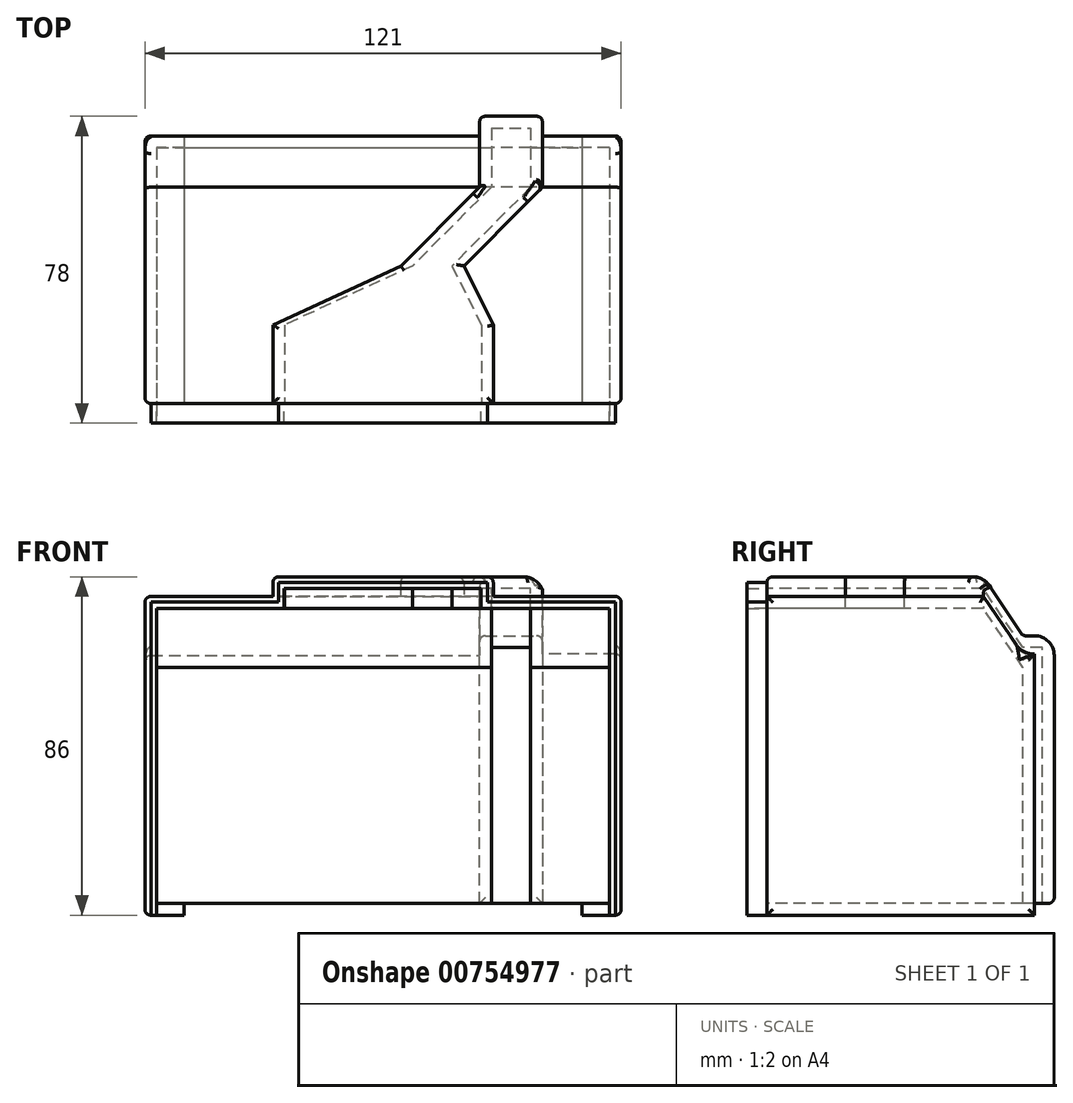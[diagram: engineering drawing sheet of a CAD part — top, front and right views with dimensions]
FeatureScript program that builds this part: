
annotation { "Feature Type Name" : "Feature", "Feature Type Description" : "" }
export const myFeature = defineFeature(function(context is Context, id is Id, definition is map)
    precondition{}
    {
        {
            var Q0;
            Q0=qCreatedBy(makeId("Front.planeOp"),FACE);
            var sketch = newSketch(context, id + "F0", { "sketchPlane" : qUnion([Q0])});
            skLineSegment(sketch, "E0", {"start": v(88, 68) * mm, "end": v(78, 68) * mm});
            skLineSegment(sketch, "E1", {"start": v(75, 71) * mm, "end": v(91, 71) * mm});
            skLineSegment(sketch, "E2", {"start": v(75, 3) * mm, "end": v(78, 3) * mm});
            skLineSegment(sketch, "E3", {"start": v(88, 3) * mm, "end": v(91, 3) * mm});
            skLineSegment(sketch, "E4", {"start": v(75, 3) * mm, "end": v(75, 71) * mm});
            skLineSegment(sketch, "E5", {"start": v(78, 3) * mm, "end": v(78, 68) * mm});
            skLineSegment(sketch, "E6", {"start": v(88, 3) * mm, "end": v(88, 68) * mm});
            skLineSegment(sketch, "E7", {"start": v(91, 71) * mm, "end": v(91, 3) * mm});
            skLineSegment(sketch, "E8", {"start": v(0, 0) * mm, "end": v(75, 0) * mm, "construction": true});
            skLineSegment(sketch, "E9", {"start": v(75, 0) * mm, "end": v(75, 3) * mm, "construction": true});
            skSolve(sketch);
        }
        {
            var Q0;
            Q0=makeQuery(id+"F0.imprint","IMPRINT",FACE,{"disambiguationData":[TD([[makeQuery(id+"F0.imprint","IMPRINT",EDGE,{"derivedFrom":sQuery(id+"F0.wireOp",EDGE,"E0")}),-1.0]])]});
            var sketch = newSketch(context, id + "F1", { "sketchPlane" : qUnion([Q0])});
            skLineSegment(sketch, "E10.0.0", {"start": v(91, 71) * mm, "end": v(75, 71) * mm});
            skLineSegment(sketch, "E10.0.1", {"start": v(75, 71) * mm, "end": v(75, 3) * mm});
            skLineSegment(sketch, "E10.0.7", {"start": v(91, 3) * mm, "end": v(91, 71) * mm});
            skLineSegment(sketch, "E11", {"start": v(91, 3) * mm, "end": v(75, 3) * mm});
            skSolve(sketch);
        }
        {
            var Q0;
            Q0 = qSketchRegion(id + "F1", true);
            extrude(context, id + "F2", {"entities" : qUnion([Q0]), "oppositeDirection" : true, "depth" : 3 * mm, "offsetDistance" : 25 * mm});
        }
        {
            var Q0;
            Q0=makeQuery(id+"F0.imprint","IMPRINT",FACE,{"disambiguationData":[TD([[makeQuery(id+"F0.imprint","IMPRINT",EDGE,{"derivedFrom":sQuery(id+"F0.wireOp",EDGE,"E0")}),-1.0]])]});
            cPlane(context, id + "F3", {"entities" : qUnion([Q0]), "cplaneType" : CPlaneType.OFFSET, "offset" : 5 * mm, "width" : 150 * mm, "height" : 150 * mm});
        }
        {
            var Q0;
            Q0=qCreatedBy(id+"F3.planeOp",FACE);
            var sketch = newSketch(context, id + "F4", { "sketchPlane" : qUnion([Q0])});
            skLineSegment(sketch, "E12", {"start": v(88, 68) * mm, "end": v(78, 68) * mm});
            skLineSegment(sketch, "E13", {"start": v(75, 71) * mm, "end": v(91, 71) * mm});
            skLineSegment(sketch, "E14", {"start": v(75, 3) * mm, "end": v(78, 3) * mm});
            skLineSegment(sketch, "E15", {"start": v(88, 3) * mm, "end": v(91, 3) * mm});
            skLineSegment(sketch, "E16", {"start": v(75, 3) * mm, "end": v(75, 71) * mm});
            skLineSegment(sketch, "E17", {"start": v(78, 3) * mm, "end": v(78, 68) * mm});
            skLineSegment(sketch, "E18", {"start": v(88, 3) * mm, "end": v(88, 68) * mm});
            skLineSegment(sketch, "E19", {"start": v(91, 71) * mm, "end": v(91, 3) * mm});
            skLineSegment(sketch, "E20", {"start": v(0, 0) * mm, "end": v(75, 0) * mm, "construction": true});
            skLineSegment(sketch, "E21", {"start": v(75, 0) * mm, "end": v(75, 3) * mm, "construction": true});
            skSolve(sketch);
        }
        {
            var Q1;
            Q1=makeQuery(id+"F1.imprint","IMPRINT",FACE,{"disambiguationData":[TD([[makeQuery(id+"F1.imprint","IMPRINT",EDGE,{"derivedFrom":sQuery(id+"F1.wireOp",EDGE,"E10.0.0")}),-1.0]])]});
            var Q2;
            Q2=makeQuery(id+"F4.imprint","IMPRINT",FACE,{"disambiguationData":[TD([[makeQuery(id+"F4.imprint","IMPRINT",EDGE,{"derivedFrom":sQuery(id+"F4.wireOp",EDGE,"E12")}),-1.0]])]});
            loft(context, id + "F5", {"operationType" : NewBodyOperationType.ADD, "sheetProfilesArray" : [{ "sheetProfileEntities" : qUnion([Q1]) }, { "sheetProfileEntities" : qUnion([Q2]) }]});
        }
        {
            var Q0;
            Q0=qCreatedBy(id+"F3.planeOp",FACE);
            var sketch = newSketch(context, id + "F6", { "sketchPlane" : qUnion([Q0])});
            skLineSegment(sketch, "E22", {"start": v(0, 3) * mm, "end": v(-7, 3) * mm});
            skLineSegment(sketch, "E23", {"start": v(-7, 3) * mm, "end": v(-7, 63) * mm});
            skLineSegment(sketch, "E24", {"start": v(108, 63) * mm, "end": v(108, 3) * mm});
            skLineSegment(sketch, "E25", {"start": v(108, 3) * mm, "end": v(101, 3) * mm});
            skLineSegment(sketch, "E26", {"start": v(101, 3) * mm, "end": v(101, 0) * mm});
            skLineSegment(sketch, "E27", {"start": v(101, 0) * mm, "end": v(111, 0) * mm});
            skLineSegment(sketch, "E28", {"start": v(111, 0) * mm, "end": v(111, 66.4) * mm});
            skLineSegment(sketch, "E29", {"start": v(-10, 66) * mm, "end": v(-10, 0) * mm});
            skLineSegment(sketch, "E30", {"start": v(-10, 0) * mm, "end": v(0, 0) * mm});
            skLineSegment(sketch, "E31", {"start": v(0, 0) * mm, "end": v(0, 3) * mm});
            skLineSegment(sketch, "E32", {"start": v(88, 68) * mm, "end": v(78, 68) * mm});
            skLineSegment(sketch, "E33", {"start": v(75, 71) * mm, "end": v(91, 71) * mm});
            skLineSegment(sketch, "E34", {"start": v(111, 66.4) * mm, "end": v(91, 66.4) * mm});
            skLineSegment(sketch, "E35", {"start": v(-10, 66) * mm, "end": v(75, 66) * mm});
            skLineSegment(sketch, "E36", {"start": v(75, 66) * mm, "end": v(75, 71) * mm});
            skLineSegment(sketch, "E37", {"start": v(91, 66.4) * mm, "end": v(91, 71) * mm});
            skLineSegment(sketch, "E38", {"start": v(108, 63) * mm, "end": v(88, 63) * mm});
            skLineSegment(sketch, "E39", {"start": v(88, 63) * mm, "end": v(88, 68) * mm});
            skLineSegment(sketch, "E40", {"start": v(-7, 63) * mm, "end": v(78, 63) * mm});
            skLineSegment(sketch, "E41", {"start": v(78, 63) * mm, "end": v(78, 68) * mm});
            skSolve(sketch);
        }
        {
            var Q0;
            Q0=makeQuery(id+"F6.imprint","IMPRINT",FACE,{"disambiguationData":[TD([[makeQuery(id+"F6.imprint","IMPRINT",EDGE,{"derivedFrom":sQuery(id+"F6.wireOp",EDGE,"E22")}),1.0]])]});
            var sketch = newSketch(context, id + "F7", { "sketchPlane" : qUnion([Q0])});
            skPoint(sketch, "E42.0", {"position": v(-10, 66) * mm});
            skPoint(sketch, "E43.0", {"position": v(75, 66) * mm});
            skPoint(sketch, "E44.0", {"position": v(91, 66.4) * mm});
            skPoint(sketch, "E45.0", {"position": v(101, 3) * mm});
            skPoint(sketch, "E46.0", {"position": v(111, 66.4) * mm});
            skLineSegment(sketch, "E47", {"start": v(-10, 66) * mm, "end": v(-10, 3) * mm});
            skLineSegment(sketch, "E48", {"start": v(75, 3) * mm, "end": v(75, 66) * mm});
            skLineSegment(sketch, "E49", {"start": v(75, 66) * mm, "end": v(-10, 66) * mm});
            skLineSegment(sketch, "E50", {"start": v(91, 66.4) * mm, "end": v(91, 3) * mm});
            skLineSegment(sketch, "E51", {"start": v(111, 3) * mm, "end": v(111, 66.4) * mm});
            skLineSegment(sketch, "E52", {"start": v(91, 66.4) * mm, "end": v(111, 66.4) * mm});
            skLineSegment(sketch, "E53", {"start": v(111, 3) * mm, "end": v(111, 0) * mm});
            skLineSegment(sketch, "E54", {"start": v(111, 0) * mm, "end": v(101, 0) * mm});
            skLineSegment(sketch, "E55", {"start": v(101, 0) * mm, "end": v(101, 3) * mm});
            skLineSegment(sketch, "E56", {"start": v(-10, 3) * mm, "end": v(-10, 0) * mm});
            skLineSegment(sketch, "E57", {"start": v(-10, 0) * mm, "end": v(0, 0) * mm});
            skLineSegment(sketch, "E58", {"start": v(0, 0) * mm, "end": v(0, 3) * mm});
            skLineSegment(sketch, "E59", {"start": v(101, 3) * mm, "end": v(91, 3) * mm});
            skLineSegment(sketch, "E60", {"start": v(75, 3) * mm, "end": v(0, 3) * mm});
            skSolve(sketch);
        }
        {
            var Q0;
            Q0=makeQuery(id+"F6.imprint","IMPRINT",FACE,{"disambiguationData":[TD([[makeQuery(id+"F6.imprint","IMPRINT",EDGE,{"derivedFrom":sQuery(id+"F6.wireOp",EDGE,"E22")}),1.0]])]});
            cPlane(context, id + "F8", {"entities" : qUnion([Q0]), "cplaneType" : CPlaneType.OFFSET, "offset" : 10 * mm, "width" : 150 * mm, "height" : 150 * mm});
        }
        {
            var Q0;
            Q0=qCreatedBy(id+"F8.planeOp",FACE);
            var sketch = newSketch(context, id + "F9", { "sketchPlane" : qUnion([Q0])});
            skLineSegment(sketch, "E61", {"start": v(0, 3) * mm, "end": v(-7, 3) * mm});
            skLineSegment(sketch, "E62", {"start": v(-7, 3) * mm, "end": v(-7, 78) * mm});
            skLineSegment(sketch, "E63", {"start": v(108, 78) * mm, "end": v(108, 3) * mm});
            skLineSegment(sketch, "E64", {"start": v(108, 3) * mm, "end": v(101, 3) * mm});
            skLineSegment(sketch, "E65", {"start": v(101, 3) * mm, "end": v(101, 0) * mm});
            skLineSegment(sketch, "E66", {"start": v(101, 0) * mm, "end": v(111, 0) * mm});
            skLineSegment(sketch, "E67", {"start": v(111, 0) * mm, "end": v(111, 81) * mm});
            skLineSegment(sketch, "E68", {"start": v(-10, 81) * mm, "end": v(-10, 0) * mm});
            skLineSegment(sketch, "E69", {"start": v(-10, 0) * mm, "end": v(0, 0) * mm});
            skLineSegment(sketch, "E70", {"start": v(0, 0) * mm, "end": v(0, 3) * mm});
            skLineSegment(sketch, "E71", {"start": v(-10, 81) * mm, "end": v(75, 81) * mm});
            skLineSegment(sketch, "E72", {"start": v(75, 81) * mm, "end": v(75, 86) * mm});
            skLineSegment(sketch, "E73", {"start": v(75, 86) * mm, "end": v(91, 86) * mm});
            skLineSegment(sketch, "E74", {"start": v(91, 86) * mm, "end": v(91, 81) * mm});
            skLineSegment(sketch, "E75", {"start": v(91, 81) * mm, "end": v(111, 81) * mm});
            skLineSegment(sketch, "E76", {"start": v(108, 78) * mm, "end": v(88, 78) * mm});
            skLineSegment(sketch, "E77", {"start": v(88, 78) * mm, "end": v(88, 83) * mm});
            skLineSegment(sketch, "E78", {"start": v(88, 83) * mm, "end": v(78, 83) * mm});
            skLineSegment(sketch, "E79", {"start": v(78, 83) * mm, "end": v(78, 78) * mm});
            skLineSegment(sketch, "E80", {"start": v(78, 78) * mm, "end": v(-7, 78) * mm});
            skSolve(sketch);
        }
        {
            var Q1;
            Q1=makeQuery(id+"F6.imprint","IMPRINT",FACE,{"disambiguationData":[TD([[makeQuery(id+"F6.imprint","IMPRINT",EDGE,{"derivedFrom":sQuery(id+"F6.wireOp",EDGE,"E22")}),1.0]])]});
            var Q2;
            Q2=makeQuery(id+"F9.imprint","IMPRINT",FACE,{"disambiguationData":[TD([[makeQuery(id+"F9.imprint","IMPRINT",EDGE,{"derivedFrom":sQuery(id+"F9.wireOp",EDGE,"E61")}),1.0]])]});
            loft(context, id + "F10", {"operationType" : NewBodyOperationType.ADD, "sheetProfilesArray" : [{ "sheetProfileEntities" : qUnion([Q1]) }, { "sheetProfileEntities" : qUnion([Q2]) }]});
        }
        {
            var Q0;
            Q0 = qSketchRegion(id + "F7", true);
            extrude(context, id + "F11", {"entities" : qUnion([Q0]), "operationType" : NewBodyOperationType.ADD, "oppositeDirection" : true, "depth" : 3 * mm, "offsetDistance" : 25 * mm});
        }
        {
            var Q0;
            Q0=makeQuery(id+"F9.imprint","IMPRINT",FACE,{"disambiguationData":[TD([[makeQuery(id+"F9.imprint","IMPRINT",EDGE,{"derivedFrom":sQuery(id+"F9.wireOp",EDGE,"E61")}),1.0]])]});
            cPlane(context, id + "F12", {"entities" : qUnion([Q0]), "cplaneType" : CPlaneType.OFFSET, "offset" : 20 * mm, "width" : 150 * mm, "height" : 150 * mm});
        }
        {
            var Q0;
            Q0=qCreatedBy(id+"F12.planeOp",FACE);
            var sketch = newSketch(context, id + "F13", { "sketchPlane" : qUnion([Q0])});
            skLineSegment(sketch, "E81", {"start": v(0, 3) * mm, "end": v(-7, 3) * mm});
            skLineSegment(sketch, "E82", {"start": v(-7, 3) * mm, "end": v(-7, 78) * mm});
            skLineSegment(sketch, "E83", {"start": v(108, 78) * mm, "end": v(108, 3) * mm});
            skLineSegment(sketch, "E84", {"start": v(108, 3) * mm, "end": v(101, 3) * mm});
            skLineSegment(sketch, "E85", {"start": v(101, 3) * mm, "end": v(101, 0) * mm});
            skLineSegment(sketch, "E86", {"start": v(101, 0) * mm, "end": v(111, 0) * mm});
            skLineSegment(sketch, "E87", {"start": v(111, 0) * mm, "end": v(111, 81) * mm});
            skLineSegment(sketch, "E88", {"start": v(-10, 81) * mm, "end": v(-10, 0) * mm});
            skLineSegment(sketch, "E89", {"start": v(-10, 0) * mm, "end": v(0, 0) * mm});
            skLineSegment(sketch, "E90", {"start": v(0, 0) * mm, "end": v(0, 3) * mm});
            skLineSegment(sketch, "E91", {"start": v(-10, 81) * mm, "end": v(55, 81) * mm});
            skLineSegment(sketch, "E92", {"start": v(55, 81) * mm, "end": v(55, 86) * mm});
            skLineSegment(sketch, "E93", {"start": v(55, 86) * mm, "end": v(71, 86) * mm});
            skLineSegment(sketch, "E94", {"start": v(71, 86) * mm, "end": v(71, 81) * mm});
            skLineSegment(sketch, "E95", {"start": v(71, 81) * mm, "end": v(111, 81) * mm});
            skLineSegment(sketch, "E96", {"start": v(108, 78) * mm, "end": v(68, 78) * mm});
            skLineSegment(sketch, "E97", {"start": v(68, 78) * mm, "end": v(68, 83) * mm});
            skLineSegment(sketch, "E98", {"start": v(68, 83) * mm, "end": v(58, 83) * mm});
            skLineSegment(sketch, "E99", {"start": v(58, 83) * mm, "end": v(58, 78) * mm});
            skLineSegment(sketch, "E100", {"start": v(58, 78) * mm, "end": v(-7, 78) * mm});
            skSolve(sketch);
        }
        {
            var Q1;
            Q1=makeQuery(id+"F9.imprint","IMPRINT",FACE,{"disambiguationData":[TD([[makeQuery(id+"F9.imprint","IMPRINT",EDGE,{"derivedFrom":sQuery(id+"F9.wireOp",EDGE,"E61")}),1.0]])]});
            var Q2;
            Q2=makeQuery(id+"F13.imprint","IMPRINT",FACE,{"disambiguationData":[TD([[makeQuery(id+"F13.imprint","IMPRINT",EDGE,{"derivedFrom":sQuery(id+"F13.wireOp",EDGE,"E81")}),1.0]])]});
            loft(context, id + "F14", {"operationType" : NewBodyOperationType.ADD, "sheetProfilesArray" : [{ "sheetProfileEntities" : qUnion([Q1]) }, { "sheetProfileEntities" : qUnion([Q2]) }]});
        }
        {
            var Q0;
            Q0=makeQuery(id+"F14.opLoft","CAP_FACE",FACE,{"disambiguationData":[OSD([makeQuery(id+"F13.imprint","IMPRINT",FACE,{"disambiguationData":[TD([[makeQuery(id+"F13.imprint","IMPRINT",EDGE,{"derivedFrom":sQuery(id+"F13.wireOp",EDGE,"E81")}),1.0]])]})])],"isStart":true});
            cPlane(context, id + "F15", {"entities" : qUnion([Q0]), "cplaneType" : CPlaneType.OFFSET, "offset" : 15 * mm, "width" : 150 * mm, "height" : 150 * mm});
        }
        {
            var Q0;
            Q0=qCreatedBy(id+"F15.planeOp",FACE);
            var sketch = newSketch(context, id + "F16", { "sketchPlane" : qUnion([Q0])});
            skLineSegment(sketch, "E101", {"start": v(0, 3) * mm, "end": v(-7, 3) * mm});
            skLineSegment(sketch, "E102", {"start": v(-7, 3) * mm, "end": v(-7, 78) * mm});
            skLineSegment(sketch, "E103", {"start": v(108, 78) * mm, "end": v(108, 3) * mm});
            skLineSegment(sketch, "E104", {"start": v(108, 3) * mm, "end": v(101, 3) * mm});
            skLineSegment(sketch, "E105", {"start": v(101, 3) * mm, "end": v(101, 0) * mm});
            skLineSegment(sketch, "E106", {"start": v(101, 0) * mm, "end": v(111, 0) * mm});
            skLineSegment(sketch, "E107", {"start": v(111, 0) * mm, "end": v(111, 81) * mm});
            skLineSegment(sketch, "E108", {"start": v(-10, 81) * mm, "end": v(-10, 0) * mm});
            skLineSegment(sketch, "E109", {"start": v(-10, 0) * mm, "end": v(0, 0) * mm});
            skLineSegment(sketch, "E110", {"start": v(0, 0) * mm, "end": v(0, 3) * mm});
            skLineSegment(sketch, "E111", {"start": v(-10, 81) * mm, "end": v(22.5, 81) * mm});
            skLineSegment(sketch, "E112", {"start": v(22.5, 81) * mm, "end": v(22.5, 86) * mm});
            skLineSegment(sketch, "E113", {"start": v(22.5, 86) * mm, "end": v(78.5, 86) * mm});
            skLineSegment(sketch, "E114", {"start": v(78.5, 86) * mm, "end": v(78.5, 81) * mm});
            skLineSegment(sketch, "E115", {"start": v(78.5, 81) * mm, "end": v(111, 81) * mm});
            skLineSegment(sketch, "E116", {"start": v(108, 78) * mm, "end": v(75.5, 78) * mm});
            skLineSegment(sketch, "E117", {"start": v(75.5, 78) * mm, "end": v(75.5, 83) * mm});
            skLineSegment(sketch, "E118", {"start": v(75.5, 83) * mm, "end": v(25.5, 83) * mm});
            skLineSegment(sketch, "E119", {"start": v(25.5, 83) * mm, "end": v(25.5, 78) * mm});
            skLineSegment(sketch, "E120", {"start": v(25.5, 78) * mm, "end": v(-7, 78) * mm});
            skSolve(sketch);
        }
        {
            var Q1;
            Q1=makeQuery(id+"F14.opLoft","CAP_FACE",FACE,{"disambiguationData":[OSD([makeQuery(id+"F13.imprint","IMPRINT",FACE,{"disambiguationData":[TD([[makeQuery(id+"F13.imprint","IMPRINT",EDGE,{"derivedFrom":sQuery(id+"F13.wireOp",EDGE,"E81")}),1.0]])]})])],"isStart":true});
            var Q2;
            Q2=makeQuery(id+"F16.imprint","IMPRINT",FACE,{"disambiguationData":[TD([[makeQuery(id+"F16.imprint","IMPRINT",EDGE,{"derivedFrom":sQuery(id+"F16.wireOp",EDGE,"E101")}),1.0]])]});
            loft(context, id + "F17", {"operationType" : NewBodyOperationType.ADD, "sheetProfilesArray" : [{ "sheetProfileEntities" : qUnion([Q1]) }, { "sheetProfileEntities" : qUnion([Q2]) }]});
        }
        {
            var Q0;
            Q0=makeQuery(id+"F17.opLoft","CAP_FACE",FACE,{"disambiguationData":[OSD([makeQuery(id+"F16.imprint","IMPRINT",FACE,{"disambiguationData":[TD([[makeQuery(id+"F16.imprint","IMPRINT",EDGE,{"derivedFrom":sQuery(id+"F16.wireOp",EDGE,"E101")}),1.0]])]})])],"isStart":true});
            cPlane(context, id + "F18", {"entities" : qUnion([Q0]), "cplaneType" : CPlaneType.OFFSET, "offset" : 20 * mm, "width" : 150 * mm, "height" : 150 * mm});
        }
        {
            var Q0;
            Q0=qCreatedBy(id+"F18.planeOp",FACE);
            var sketch = newSketch(context, id + "F19", { "sketchPlane" : qUnion([Q0])});
            skLineSegment(sketch, "E121", {"start": v(0, 3) * mm, "end": v(-7, 3) * mm});
            skLineSegment(sketch, "E122", {"start": v(-7, 3) * mm, "end": v(-7, 78) * mm});
            skLineSegment(sketch, "E123", {"start": v(108, 78) * mm, "end": v(108, 3) * mm});
            skLineSegment(sketch, "E124", {"start": v(108, 3) * mm, "end": v(101, 3) * mm});
            skLineSegment(sketch, "E125", {"start": v(101, 3) * mm, "end": v(101, 0) * mm});
            skLineSegment(sketch, "E126", {"start": v(101, 0) * mm, "end": v(111, 0) * mm});
            skLineSegment(sketch, "E127", {"start": v(111, 0) * mm, "end": v(111, 81) * mm});
            skLineSegment(sketch, "E128", {"start": v(-10, 81) * mm, "end": v(-10, 0) * mm});
            skLineSegment(sketch, "E129", {"start": v(-10, 0) * mm, "end": v(0, 0) * mm});
            skLineSegment(sketch, "E130", {"start": v(0, 0) * mm, "end": v(0, 3) * mm});
            skLineSegment(sketch, "E131", {"start": v(-10, 81) * mm, "end": v(22.5, 81) * mm});
            skLineSegment(sketch, "E132", {"start": v(22.5, 81) * mm, "end": v(22.5, 86) * mm});
            skLineSegment(sketch, "E133", {"start": v(22.5, 86) * mm, "end": v(78.5, 86) * mm});
            skLineSegment(sketch, "E134", {"start": v(78.5, 86) * mm, "end": v(78.5, 81) * mm});
            skLineSegment(sketch, "E135", {"start": v(78.5, 81) * mm, "end": v(111, 81) * mm});
            skLineSegment(sketch, "E136", {"start": v(108, 78) * mm, "end": v(75.5, 78) * mm});
            skLineSegment(sketch, "E137", {"start": v(75.5, 78) * mm, "end": v(75.5, 83) * mm});
            skLineSegment(sketch, "E138", {"start": v(75.5, 83) * mm, "end": v(25.5, 83) * mm});
            skLineSegment(sketch, "E139", {"start": v(25.5, 83) * mm, "end": v(25.5, 78) * mm});
            skLineSegment(sketch, "E140", {"start": v(25.5, 78) * mm, "end": v(-7, 78) * mm});
            skSolve(sketch);
        }
        {
            var Q1;
            Q1=makeQuery(id+"F17.opLoft","CAP_FACE",FACE,{"disambiguationData":[OSD([makeQuery(id+"F16.imprint","IMPRINT",FACE,{"disambiguationData":[TD([[makeQuery(id+"F16.imprint","IMPRINT",EDGE,{"derivedFrom":sQuery(id+"F16.wireOp",EDGE,"E101")}),1.0]])]})])],"isStart":true});
            var Q2;
            Q2=makeQuery(id+"F19.imprint","IMPRINT",FACE,{"disambiguationData":[TD([[makeQuery(id+"F19.imprint","IMPRINT",EDGE,{"derivedFrom":sQuery(id+"F19.wireOp",EDGE,"E121")}),1.0]])]});
            loft(context, id + "F20", {"operationType" : NewBodyOperationType.ADD, "sheetProfilesArray" : [{ "sheetProfileEntities" : qUnion([Q1]) }, { "sheetProfileEntities" : qUnion([Q2]) }]});
        }
        {
            var Q0;
            Q0=qCreatedBy(id+"F18.planeOp",FACE);
            var sketch = newSketch(context, id + "F21", { "sketchPlane" : qUnion([Q0])});
            skLineSegment(sketch, "E141", {"start": v(-7, 3) * mm, "end": v(-7, 78) * mm});
            skLineSegment(sketch, "E142", {"start": v(108, 78) * mm, "end": v(108, 3) * mm});
            skLineSegment(sketch, "E143", {"start": v(109.5, 0) * mm, "end": v(109.5, 79.6) * mm});
            skLineSegment(sketch, "E144", {"start": v(-8.5, 79.6) * mm, "end": v(-8.5, 0) * mm});
            skLineSegment(sketch, "E145", {"start": v(-8.5, 79.6) * mm, "end": v(23.9, 79.6) * mm});
            skLineSegment(sketch, "E146", {"start": v(23.9, 79.6) * mm, "end": v(23.9, 84.5) * mm});
            skLineSegment(sketch, "E147", {"start": v(23.9, 84.5) * mm, "end": v(77, 84.5) * mm});
            skLineSegment(sketch, "E148", {"start": v(77, 84.5) * mm, "end": v(77, 79.6) * mm});
            skLineSegment(sketch, "E149", {"start": v(77, 79.6) * mm, "end": v(109.5, 79.6) * mm});
            skLineSegment(sketch, "E150", {"start": v(108, 78) * mm, "end": v(75.4, 78) * mm});
            skLineSegment(sketch, "E151", {"start": v(75.4, 78) * mm, "end": v(75.4, 83) * mm});
            skLineSegment(sketch, "E152", {"start": v(75.4, 83) * mm, "end": v(25.4, 83) * mm});
            skLineSegment(sketch, "E153", {"start": v(25.4, 83) * mm, "end": v(25.4, 78) * mm});
            skLineSegment(sketch, "E154", {"start": v(25.4, 78) * mm, "end": v(-7, 78) * mm});
            skLineSegment(sketch, "E155", {"start": v(-8.5, 0) * mm, "end": v(-7, 0) * mm});
            skLineSegment(sketch, "E156", {"start": v(-7, 0) * mm, "end": v(-7, 3) * mm});
            skLineSegment(sketch, "E157", {"start": v(-7, 0) * mm, "end": v(0, 0) * mm, "construction": true});
            skLineSegment(sketch, "E158", {"start": v(109.5, 0) * mm, "end": v(108, 0) * mm});
            skLineSegment(sketch, "E159", {"start": v(108, 0) * mm, "end": v(108, 3) * mm});
            skSolve(sketch);
        }
        {
            var Q0;
            Q0 = qSketchRegion(id + "F21", true);
            extrude(context, id + "F22", {"entities" : qUnion([Q0]), "operationType" : NewBodyOperationType.ADD, "depth" : 5 * mm, "offsetDistance" : 25 * mm});
        }
        {
            var Q0;
            {var subQ0=sQuery(id+"F16.wireOp",EDGE,"E111");var subQ1=sQuery(id+"F16.wireOp",EDGE,"E109");var subQ2=sQuery(id+"F16.wireOp",EDGE,"E108");var subQ3=sQuery(id+"F13.wireOp",EDGE,"E91");var subQ4=sQuery(id+"F13.wireOp",EDGE,"E89");var subQ5=sQuery(id+"F13.wireOp",EDGE,"E88");var subQ6=sQuery(id+"F9.wireOp",EDGE,"E71");var subQ7=sQuery(id+"F9.wireOp",EDGE,"E69");var subQ8=sQuery(id+"F9.wireOp",EDGE,"E68");Q0=makeQuery(id+"F20.boolean.opBoolean","MERGE",FACE,{"derivedFrom":[makeQuery(id+"F17.boolean.opBoolean","MERGE",FACE,{"derivedFrom":[makeQuery(id+"F14.boolean.opBoolean","MERGE",FACE,{"derivedFrom":[makeQuery(id+"F11.boolean.opBoolean","MERGE",FACE,{"derivedFrom":[makeQuery(id+"F10.opLoft","SWEPT_FACE",FACE,{"disambiguationData":[OSD([sQuery(id+"F6.wireOp",EDGE,"E29"),sQuery(id+"F6.wireOp",EDGE,"E30"),sQuery(id+"F6.wireOp",EDGE,"E35"),subQ8,subQ7,subQ6])]}),makeQuery(id+"F11.opExtrude","SWEPT_FACE",FACE,{"disambiguationData":[OSD([sQuery(id+"F7.wireOp",EDGE,"E47"),sQuery(id+"F7.wireOp",EDGE,"E56")])]})]}),makeQuery(id+"F14.opLoft","SWEPT_FACE",FACE,{"disambiguationData":[OSD([subQ8,subQ7,subQ6,subQ5,subQ4,subQ3])]})]}),makeQuery(id+"F17.opLoft","SWEPT_FACE",FACE,{"disambiguationData":[OSD([subQ5,subQ4,subQ3,subQ2,subQ1,subQ0])]})]}),makeQuery(id+"F20.opLoft","SWEPT_FACE",FACE,{"disambiguationData":[OSD([subQ2,subQ1,subQ0,sQuery(id+"F19.wireOp",EDGE,"E128"),sQuery(id+"F19.wireOp",EDGE,"E129"),sQuery(id+"F19.wireOp",EDGE,"E131")])]})]});}
            var Q1;
            {var subQ0=sQuery(id+"F16.wireOp",EDGE,"E115");var subQ1=sQuery(id+"F16.wireOp",EDGE,"E107");var subQ2=sQuery(id+"F16.wireOp",EDGE,"E106");var subQ3=sQuery(id+"F13.wireOp",EDGE,"E95");var subQ4=sQuery(id+"F13.wireOp",EDGE,"E87");var subQ5=sQuery(id+"F13.wireOp",EDGE,"E86");var subQ6=sQuery(id+"F9.wireOp",EDGE,"E75");var subQ7=sQuery(id+"F9.wireOp",EDGE,"E67");var subQ8=sQuery(id+"F9.wireOp",EDGE,"E66");Q1=makeQuery(id+"F20.boolean.opBoolean","MERGE",FACE,{"derivedFrom":[makeQuery(id+"F17.boolean.opBoolean","MERGE",FACE,{"derivedFrom":[makeQuery(id+"F14.boolean.opBoolean","MERGE",FACE,{"derivedFrom":[makeQuery(id+"F11.boolean.opBoolean","MERGE",FACE,{"derivedFrom":[makeQuery(id+"F10.opLoft","SWEPT_FACE",FACE,{"disambiguationData":[OSD([sQuery(id+"F6.wireOp",EDGE,"E27"),sQuery(id+"F6.wireOp",EDGE,"E28"),sQuery(id+"F6.wireOp",EDGE,"E34"),subQ8,subQ7,subQ6])]}),makeQuery(id+"F11.opExtrude","SWEPT_FACE",FACE,{"disambiguationData":[OSD([sQuery(id+"F7.wireOp",EDGE,"E51"),sQuery(id+"F7.wireOp",EDGE,"E53")])]})]}),makeQuery(id+"F14.opLoft","SWEPT_FACE",FACE,{"disambiguationData":[OSD([subQ8,subQ7,subQ6,subQ5,subQ4,subQ3])]})]}),makeQuery(id+"F17.opLoft","SWEPT_FACE",FACE,{"disambiguationData":[OSD([subQ5,subQ4,subQ3,subQ2,subQ1,subQ0])]})]}),makeQuery(id+"F20.opLoft","SWEPT_FACE",FACE,{"disambiguationData":[OSD([subQ2,subQ1,subQ0,sQuery(id+"F19.wireOp",EDGE,"E126"),sQuery(id+"F19.wireOp",EDGE,"E127"),sQuery(id+"F19.wireOp",EDGE,"E135")])]})]});}
            fillet(context, id + "F23", {"entities" : qUnion([Q0, Q1]), "radius" : 1.5 * mm, "tangentPropagation" : true, "allowEdgeOverflow" : false});
        }
        {
            var Q0;
            Q0=makeQuery(id+"F2.opExtrude","CAP_EDGE",EDGE,{"disambiguationData":[OSD([sQuery(id+"F1.wireOp",EDGE,"E10.0.0")])],"isStart":false});
            var Q1;
            {var subQ0=sQuery(id+"F9.wireOp",EDGE,"E74");var subQ1=sQuery(id+"F9.wireOp",EDGE,"E73");var subQ2=sQuery(id+"F9.wireOp",EDGE,"E72");Q1=makeQuery(id+"F14.boolean.opBoolean","MERGE",EDGE,{"derivedFrom":[makeQuery(id+"F10.opLoft","MID_CAP_EDGE",EDGE,{"disambiguationData":[OSD([subQ2,subQ1,subQ0])],"capPos":1.0}),makeQuery(id+"F14.opLoft","MID_CAP_EDGE",EDGE,{"disambiguationData":[OSD([subQ2,subQ1,subQ0])],"capPos":0.0})]});}
            fillet(context, id + "F24", {"entities" : qUnion([Q0, Q1]), "radius" : 5 * mm, "tangentPropagation" : true, "allowEdgeOverflow" : false});
        }
        {
            var Q0;
            Q0=makeQuery(id+"F2.opExtrude","CAP_FACE",FACE,{"disambiguationData":[OSD([sQuery(id+"F1.wireOp",EDGE,"E10.0.0"),sQuery(id+"F1.wireOp",EDGE,"E10.0.1"),sQuery(id+"F1.wireOp",EDGE,"E10.0.7"),sQuery(id+"F1.wireOp",EDGE,"E11")])],"isStart":false});
            var Q1;
            Q1=makeQuery(id+"F10.opLoft","SWEPT_FACE",FACE,{"disambiguationData":[OSD([sQuery(id+"F6.wireOp",EDGE,"E33"),sQuery(id+"F6.wireOp",EDGE,"E36"),sQuery(id+"F6.wireOp",EDGE,"E37"),sQuery(id+"F9.wireOp",EDGE,"E72"),sQuery(id+"F9.wireOp",EDGE,"E73"),sQuery(id+"F9.wireOp",EDGE,"E74")])]});
            var Q2;
            {var subQ0=sQuery(id+"F16.wireOp",EDGE,"E114");var subQ1=sQuery(id+"F16.wireOp",EDGE,"E113");var subQ2=sQuery(id+"F16.wireOp",EDGE,"E112");var subQ3=sQuery(id+"F13.wireOp",EDGE,"E94");var subQ4=sQuery(id+"F13.wireOp",EDGE,"E93");var subQ5=sQuery(id+"F13.wireOp",EDGE,"E92");Q2=makeQuery(id+"F20.boolean.opBoolean","MERGE",FACE,{"derivedFrom":[makeQuery(id+"F17.boolean.opBoolean","MERGE",FACE,{"derivedFrom":[makeQuery(id+"F14.opLoft","SWEPT_FACE",FACE,{"disambiguationData":[OSD([sQuery(id+"F9.wireOp",EDGE,"E72"),sQuery(id+"F9.wireOp",EDGE,"E73"),sQuery(id+"F9.wireOp",EDGE,"E74"),subQ5,subQ4,subQ3])]}),makeQuery(id+"F17.opLoft","SWEPT_FACE",FACE,{"disambiguationData":[OSD([subQ5,subQ4,subQ3,subQ2,subQ1,subQ0])]})]}),makeQuery(id+"F20.opLoft","SWEPT_FACE",FACE,{"disambiguationData":[OSD([subQ2,subQ1,subQ0,sQuery(id+"F19.wireOp",EDGE,"E132"),sQuery(id+"F19.wireOp",EDGE,"E133"),sQuery(id+"F19.wireOp",EDGE,"E134")])]})]});}
            fillet(context, id + "F25", {"entities" : qUnion([Q0, Q1, Q2]), "radius" : 1.5 * mm, "tangentPropagation" : true, "allowEdgeOverflow" : false});
        }
        {
            var Q0;
            Q0=makeQuery(id+"F11.boolean.opBoolean","MERGE",EDGE,{"derivedFrom":[makeQuery(id+"F10.opLoft","MID_CAP_EDGE",EDGE,{"disambiguationData":[OSD([sQuery(id+"F6.wireOp",EDGE,"E28"),sQuery(id+"F6.wireOp",EDGE,"E34"),sQuery(id+"F6.wireOp",EDGE,"E37")])],"capPos":0.0}),makeQuery(id+"F11.opExtrude","CAP_EDGE",EDGE,{"disambiguationData":[OSD([sQuery(id+"F7.wireOp",EDGE,"E52")])],"isStart":true})]});
            var Q1;
            Q1=makeQuery(id+"F11.boolean.opBoolean","MERGE",EDGE,{"derivedFrom":[makeQuery(id+"F10.opLoft","MID_CAP_EDGE",EDGE,{"disambiguationData":[OSD([sQuery(id+"F6.wireOp",EDGE,"E29"),sQuery(id+"F6.wireOp",EDGE,"E35"),sQuery(id+"F6.wireOp",EDGE,"E36")])],"capPos":0.0}),makeQuery(id+"F11.opExtrude","CAP_EDGE",EDGE,{"disambiguationData":[OSD([sQuery(id+"F7.wireOp",EDGE,"E49")])],"isStart":true})]});
            fillet(context, id + "F26", {"entities" : qUnion([Q0, Q1]), "radius" : 5 * mm, "tangentPropagation" : true, "allowEdgeOverflow" : false});
        }
    });
